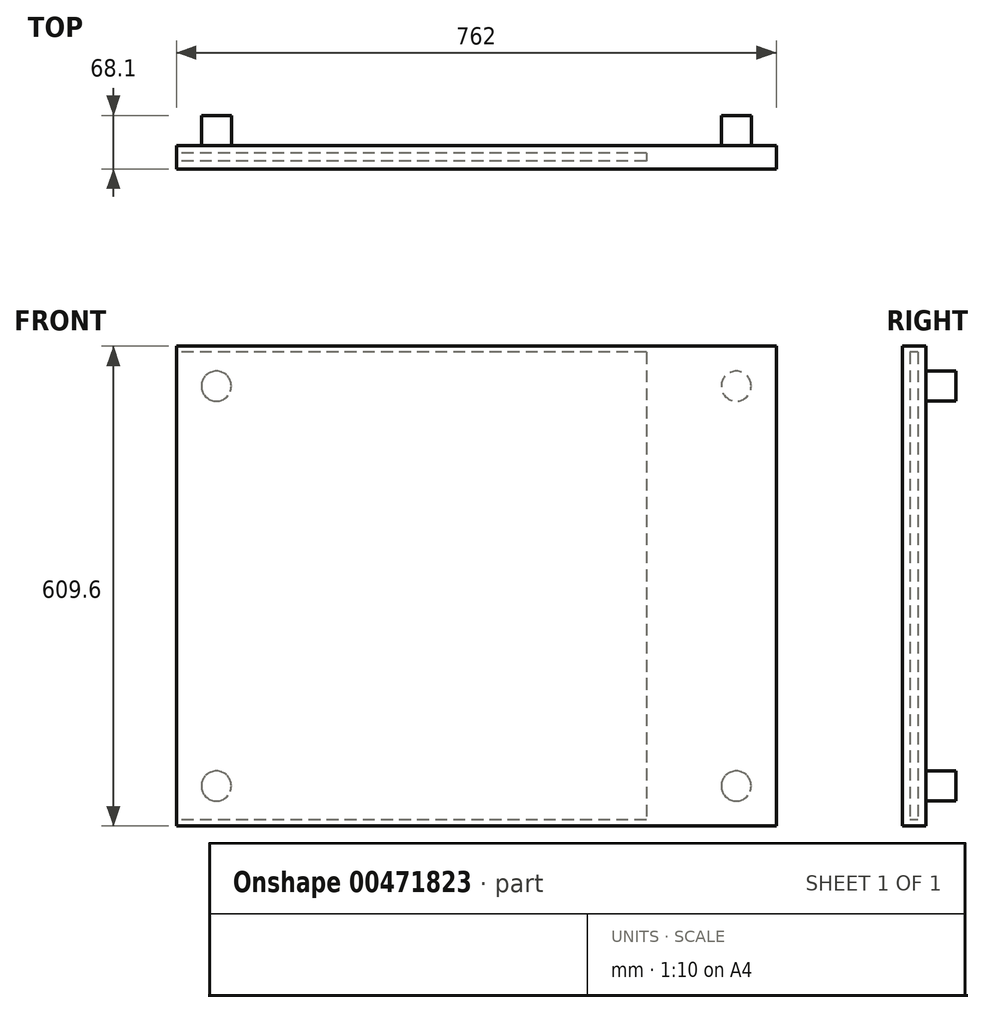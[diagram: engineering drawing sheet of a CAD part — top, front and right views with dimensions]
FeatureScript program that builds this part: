
annotation { "Feature Type Name" : "Feature", "Feature Type Description" : "" }
export const myFeature = defineFeature(function(context is Context, id is Id, definition is map)
    precondition{}
    {
        {
            var Q0;
            Q0=qCreatedBy(makeId("Front.planeOp"),FACE);
            var sketch = newSketch(context, id + "F0", { "sketchPlane" : qUnion([Q0])});
            skLineSegment(sketch, "E0.bottom", {"start": v(381, -304.8) * mm, "end": v(-381, -304.8) * mm});
            skLineSegment(sketch, "E0.top", {"start": v(381, 304.8) * mm, "end": v(-381, 304.8) * mm});
            skLineSegment(sketch, "E0.left", {"start": v(381, -304.8) * mm, "end": v(381, 304.8) * mm});
            skLineSegment(sketch, "E0.right", {"start": v(-381, -304.8) * mm, "end": v(-381, 304.8) * mm});
            skPoint(sketch, "E0.middle", {"position": v(0, 0) * mm});
            skSolve(sketch);
        }
        {
            var Q0;
            Q0=makeQuery(id+"F0.imprint","IMPRINT",FACE,{"disambiguationData":[TD([[makeQuery(id+"F0.imprint","IMPRINT",EDGE,{"derivedFrom":sQuery(id+"F0.wireOp",EDGE,"E0.bottom")}),-1.0]])]});
            extrude(context, id + "F1", {"entities" : qUnion([Q0]), "depth" : 30 * mm});
        }
        {
            var Q0;
            Q0=makeQuery(id+"F1.opExtrude","SWEPT_FACE",FACE,{"disambiguationData":[OSD([sQuery(id+"F0.wireOp",EDGE,"E0.right")])]});
            var sketch = newSketch(context, id + "F2", { "sketchPlane" : qUnion([Q0])});
            skLineSegment(sketch, "E1.bottom", {"start": v(10, 297.18) * mm, "end": v(20, 297.18) * mm});
            skLineSegment(sketch, "E1.top", {"start": v(10, -297.18) * mm, "end": v(20, -297.18) * mm});
            skLineSegment(sketch, "E1.left", {"start": v(10, 297.18) * mm, "end": v(10, -297.18) * mm});
            skLineSegment(sketch, "E1.right", {"start": v(20, 297.18) * mm, "end": v(20, -297.18) * mm});
            skSolve(sketch);
        }
        {
            var Q0;
            Q0=makeQuery(id+"F2.imprint","IMPRINT",FACE,{"disambiguationData":[TD([[makeQuery(id+"F2.imprint","IMPRINT",EDGE,{"derivedFrom":sQuery(id+"F2.wireOp",EDGE,"E1.bottom")}),-1.0]])]});
            extrude(context, id + "F3", {"entities" : qUnion([Q0]), "operationType" : NewBodyOperationType.REMOVE, "oppositeDirection" : true, "depth" : 596.9 * mm});
        }
        {
            var Q0;
            Q0=makeQuery(id+"F1.opExtrude","CAP_FACE",FACE,{"disambiguationData":[OSD([sQuery(id+"F0.wireOp",EDGE,"E0.bottom"),sQuery(id+"F0.wireOp",EDGE,"E0.top"),sQuery(id+"F0.wireOp",EDGE,"E0.left"),sQuery(id+"F0.wireOp",EDGE,"E0.right")])],"isStart":true});
            var sketch = newSketch(context, id + "F4", { "sketchPlane" : qUnion([Q0])});
            skCircle(sketch, "E2", {"center": v(-330.2, 254) * mm, "radius": 19.05 * mm});
            skCircle(sketch, "E3", {"center": v(330.2, 254) * mm, "radius": 19.05 * mm});
            skCircle(sketch, "E4", {"center": v(330.2, -254) * mm, "radius": 19.05 * mm});
            skCircle(sketch, "E5", {"center": v(-330.2, -254) * mm, "radius": 19.05 * mm});
            skSolve(sketch);
        }
        {
            var Q0;
            Q0=qSketchRegion(id+"F4",true);
            extrude(context, id + "F5", {"entities" : qUnion([Q0]), "operationType" : NewBodyOperationType.ADD, "depth" : 38.1 * mm});
        }
    });
